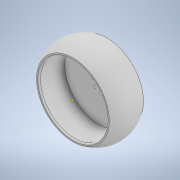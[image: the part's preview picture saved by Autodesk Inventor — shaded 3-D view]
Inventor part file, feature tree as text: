
AUTODESK INVENTOR PART (.ipt)
format: ipt  version: 2020 (Build 240168000, 168)  size: 412,672 bytes
history: native  units: mm
features: sketch x6, other x4, extrude x3, reference x2, sweep x1, shell x1, fillet x1, projected_geometry x1
ambient origin geometry x8: Origin, YZ Plane, XZ Plane, XY Plane, X Axis, Y Axis, Z Axis, Center Point
bodies: Solid1 (feature_tree)
feature tree (19):
  sweep  "Sweep1"
  shell  "Shell1"  Thickness=12.0mm
  extrude  "Extrusion1"  Depth=15.0mm
  extrude  "Extrusion2"  Depth=2.5mm
  extrude  "Extrusion3"  Depth=10.0mm
  fillet  "Fillet1"  Radius=10.0mm
  sketch  "Sketch8"  dims[d15=1.0mm]
  sketch  "Sketch1"  dims[d0=75.0mm d1=50.0mm d2=12.0mm]
  sketch  "Sketch2"  dims[d3=30.0mm d4=15.0mm]
  sketch  "Sketch4"  dims[d5=0.0mm d6=0.0mm d7=2.5mm]
  reference  "Reference1"
  reference  "Reference2"
  sketch  "Sketch6"  dims[d8=10.0mm d9=0.0mm d10=5.0mm d11=10.0mm d12=0.0mm]
  sketch  "Sketch7"  dims[d13=4.0mm d14=0.0mm]
  projected_geometry  "Projected Loop1"
  other  "<userpath>\Desktop\KangKangBalancing\KangKang.iam"
  other  "KangKang.iam"
  other  "tarot_5008_340kv_assy:1"
  other  "housing0:1"
